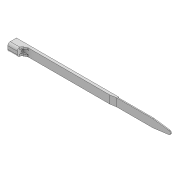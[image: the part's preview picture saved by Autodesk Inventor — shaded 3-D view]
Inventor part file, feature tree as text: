
AUTODESK INVENTOR PART (.ipt)
format: ipt  version: 2022 (Build 260153000, 153)  size: 566,784 bytes
history: native  units: in
note: dims shown in document units (in); Inventor stores cm internally (conversion verified against a paired STEP export)
features: extrude x11, sketch x10, projected_geometry x9, fillet x4, other x2, plane x1, pattern_linear x1
ambient origin geometry x8: Origin, YZ Plane, XZ Plane, XY Plane, X Axis, Y Axis, Z Axis, Center Point
bodies: Solid1 (feature_tree)
feature tree (38):
  other  "Cable_Tie1"
  other  "MeshFeature1"
  extrude  "Extrusion1"  Depth=0.0079in
  fillet  "Fillet1"  Radius=3.937in
  fillet  "Fillet2"  Radius=0.0984in
  plane  "Work Plane1"
  extrude  "Extrusion2"  Depth=0.063in
  extrude  "Extrusion4"  Depth=17.3228in
  extrude  "Extrusion12"  Depth=3.1496in
  pattern_linear  "Rectangular Pattern1"  Count1=10 Spacing1=0.0in
  extrude  "Extrusion5"  Depth=0.1969in TaperAngle=0.0deg
  extrude  "Extrusion6"  Depth=3.937in TaperAngle=0.0deg
  extrude  "Extrusion7"  Depth=0.0787in
  extrude  "Extrusion8"  Depth=0.0236in TaperAngle=0.0deg
  fillet  "Fillet3"  Radius=0.1575in
  extrude  "Extrusion9"  Depth=0.063in TaperAngle=0.0deg
  extrude  "Extrusion10"  Depth=0.0787in TaperAngle=0.0deg
  extrude  "Extrusion11"  Depth=0.0787in TaperAngle=0.0deg
  fillet  "Fillet4"  [1 undecoded]
  sketch  "Sketch1"  dims[d0=0.0709in d1=0.0in d2=0.0079in d3=3.937in d4=0.0984in d5=0.0in]
  sketch  "Sketch2"  dims[d9=0.0197in d10=0.063in]
  projected_geometry  "Projected Loop1"
  sketch  "Sketch4"  dims[d11=0.1575in d12=0.0in d13=17.3228in d15=0.126in]
  projected_geometry  "Projected Loop2"
  projected_geometry  "Projected Loop3"
  sketch  "Sketch5"  dims[d16=3.937in d17=0.0in d19=3.1496in d20=3.937in d21=0.0in]
  projected_geometry  "Projected Loop4"
  sketch  "Sketch7"  dims[d22=0.315in d23=0.1969in d24=0.0in]
  projected_geometry  "Projected Loop5"
  sketch  "Sketch8"  dims[d25=0.0591in d26=3.937in d27=0.0in]
  projected_geometry  "Projected Loop6"
  sketch  "Sketch10"  dims[d28=0.0197in d29=0.0787in]
  sketch  "Sketch13"  dims[d30=0.1969in d31=0.0236in d32=0.0in d36=0.1575in]
  sketch  "Sketch14"  dims[d37=0.063in d38=0.0in d39=0.063in d40=0.0in]
  projected_geometry  "Projected Loop10"
  sketch  "Sketch18"  dims[d41=0.0787in d42=0.0866in d43=0.0in d44=0.0157in d45=0.0in]
  projected_geometry  "Projected Loop14"
  projected_geometry  "Projected Loop15"
note: 1 required parameter value undecoded (feature->parameter linkage not recoverable at this tier; creation-order binding heuristic only, values carry confidence <= 0.55)
